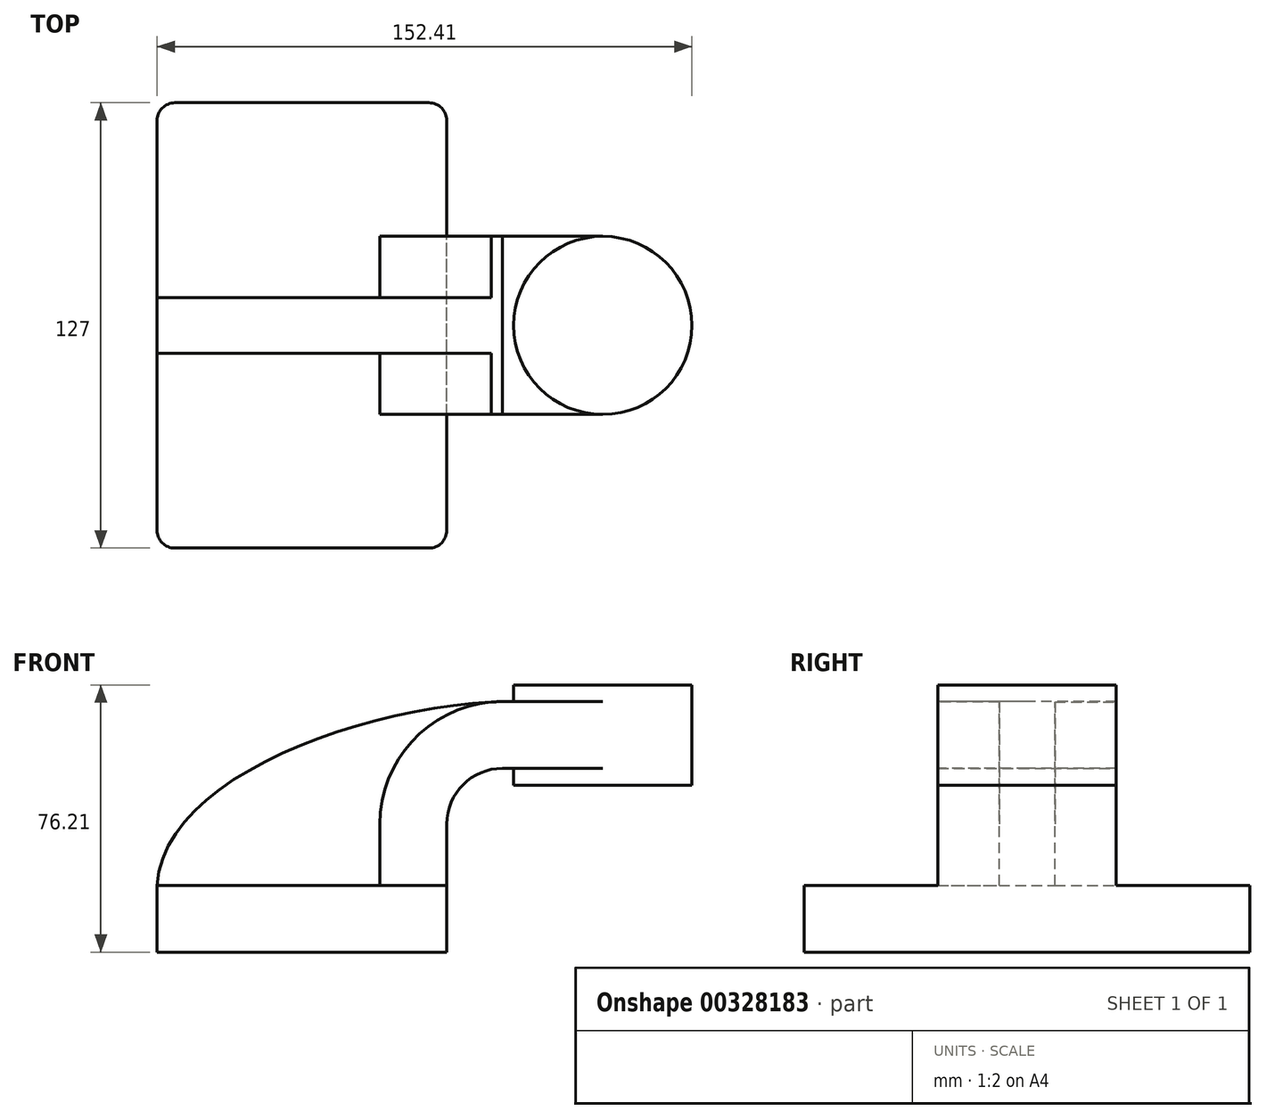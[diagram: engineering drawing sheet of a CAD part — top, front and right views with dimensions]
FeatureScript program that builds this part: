
annotation { "Feature Type Name" : "Feature", "Feature Type Description" : "" }
export const myFeature = defineFeature(function(context is Context, id is Id, definition is map)
    precondition{}
    {
        {
            var Q0;
            Q0=qCreatedBy(makeId("Front.planeOp"),FACE);
            var sketch = newSketch(context, id + "F0", { "sketchPlane" : qUnion([Q0])});
            skLineSegment(sketch, "E0.rect.bottom", {"start": v(-41.28, 9.52) * mm, "end": v(41.28, 9.52) * mm});
            skLineSegment(sketch, "E0.rect.top", {"start": v(-41.28, -9.52) * mm, "end": v(41.28, -9.52) * mm});
            skLineSegment(sketch, "E0.rect.left", {"start": v(-41.28, 9.52) * mm, "end": v(-41.28, -9.52) * mm});
            skLineSegment(sketch, "E0.rect.right", {"start": v(41.28, 9.52) * mm, "end": v(41.28, -9.52) * mm});
            skPoint(sketch, "E0.rect.middle", {"position": v(0, 0) * mm});
            skLineSegment(sketch, "E1", {"start": v(41.28, 9.52) * mm, "end": v(41.28, 27) * mm});
            skArc(sketch, "E2", {"start": v(41.28, 27) * mm, "mid": v(45.92, 38.23) * mm, "end": v(57.15, 42.88) * mm});
            skLineSegment(sketch, "E3", {"start": v(57.15, 42.88) * mm, "end": v(85.72, 42.88) * mm});
            skLineSegment(sketch, "E4.rect.bottom", {"start": v(60.32, 38.1) * mm, "end": v(111.12, 38.1) * mm});
            skLineSegment(sketch, "E4.rect.top", {"start": v(60.32, 66.68) * mm, "end": v(111.12, 66.68) * mm});
            skLineSegment(sketch, "E4.rect.left", {"start": v(60.32, 38.1) * mm, "end": v(60.32, 66.68) * mm});
            skLineSegment(sketch, "E4.rect.right", {"start": v(111.13, 38.1) * mm, "end": v(111.12, 66.68) * mm});
            skPoint(sketch, "E4.rect.middle", {"position": v(85.72, 52.39) * mm});
            skLineSegment(sketch, "E5.0", {"start": v(57.15, 61.93) * mm, "end": v(85.72, 61.93) * mm});
            skArc(sketch, "E5.1", {"start": v(22.23, 27) * mm, "mid": v(32.45, 51.7) * mm, "end": v(57.15, 61.93) * mm});
            skLineSegment(sketch, "E5.2", {"start": v(22.23, 9.52) * mm, "end": v(22.23, 27) * mm});
            skLineSegment(sketch, "E6", {"start": v(85.72, 38.1) * mm, "end": v(85.72, 66.68) * mm});
            skFitSpline(sketch, "E7", {"points": [v(-41.28, 9.53) * mm, v(57.15, 61.93) * mm], "startDerivative": vector(5.2, 92.34) * mm, "endDerivative": vector(120.92, 4.22) * mm});
            skSolve(sketch);
        }
        {
            var Q0;
            Q0=makeQuery(id+"F0.imprint","IMPRINT",FACE,{"disambiguationData":[TD([[makeQuery(id+"F0.imprint","IMPRINT",EDGE,{"derivedFrom":sQuery(id+"F0.wireOp",EDGE,"E0.rect.top")}),1.0]])]});
            extrude(context, id + "F1", {"entities" : qUnion([Q0]), "endBound" : BoundingType.SYMMETRIC, "depth" : 127 * mm});
        }
        {
            var Q0;
            {var subQ9=sQuery(id+"F0.wireOp",EDGE,"E1");Q0=makeQuery(id+"F0.imprint","IMPRINT",FACE,{"disambiguationData":[TD([[makeQuery(id+"F0.imprint","IMPRINT",EDGE,{"derivedFrom":subQ9}),1.0]])]});}
            var Q1;
            {var subQ0=sQuery(id+"F0.wireOp",EDGE,"E6");var subQ1=sQuery(id+"F0.wireOp",EDGE,"E3");var subQ2=makeQuery(id+"F0.imprint","INTERSECT",VERTEX,{"derivedFrom":[subQ1,subQ0]});Q1=makeQuery(id+"F0.imprint","IMPRINT",FACE,{"disambiguationData":[TD([[makeQuery(id+"F0.imprint","IMPRINT",EDGE,{"disambiguationData":[TD([[subQ2,1.0]])],"derivedFrom":subQ1}),1.0]])]});}
            extrude(context, id + "F2", {"entities" : qUnion([Q0, Q1]), "operationType" : NewBodyOperationType.ADD, "endBound" : BoundingType.SYMMETRIC, "depth" : 50.8 * mm});
        }
        {
            var Q0;
            {var subQ3=sQuery(id+"F0.wireOp",EDGE,"E5.2");Q0=makeQuery(id+"F0.imprint","IMPRINT",FACE,{"disambiguationData":[TD([[makeQuery(id+"F0.imprint","IMPRINT",EDGE,{"derivedFrom":subQ3}),1.0]])]});}
            extrude(context, id + "F3", {"entities" : qUnion([Q0]), "operationType" : NewBodyOperationType.ADD, "endBound" : BoundingType.SYMMETRIC, "depth" : 15.88 * mm});
        }
        {
            var Q0;
            {var subQ5=sQuery(id+"F0.wireOp",EDGE,"E4.rect.right");Q0=makeQuery(id+"F0.imprint","IMPRINT",FACE,{"disambiguationData":[TD([[makeQuery(id+"F0.imprint","IMPRINT",EDGE,{"derivedFrom":subQ5}),1.0]])]});}
            var Q1;
            Q1=sQuery(id+"F0.wireOp",EDGE,"E6");
            revolve(context, id + "F4", {"operationType" : NewBodyOperationType.ADD, "entities" : qUnion([Q0]), "axis" : qUnion([Q1]), "revolveType" : RevolveType.FULL});
        }
        {
            var Q0;
            Q0=makeQuery(id+"F1.opExtrude","CAP_EDGE",EDGE,{"disambiguationData":[OSD([sQuery(id+"F0.wireOp",EDGE,"E0.rect.right")])],"isStart":false});
            var Q1;
            Q1=makeQuery(id+"F1.opExtrude","CAP_EDGE",EDGE,{"disambiguationData":[OSD([sQuery(id+"F0.wireOp",EDGE,"E0.rect.left")])],"isStart":false});
            var Q2;
            Q2=makeQuery(id+"F1.opExtrude","CAP_EDGE",EDGE,{"disambiguationData":[OSD([sQuery(id+"F0.wireOp",EDGE,"E0.rect.right")])],"isStart":true});
            var Q3;
            Q3=makeQuery(id+"F1.opExtrude","CAP_EDGE",EDGE,{"disambiguationData":[OSD([sQuery(id+"F0.wireOp",EDGE,"E0.rect.left")])],"isStart":true});
            fillet(context, id + "F5", {"entities" : qUnion([Q0, Q1, Q2, Q3]), "radius" : 5.08 * mm, "tangentPropagation" : true, "allowEdgeOverflow" : false});
        }
        {
            var Q0;
            Q0=makeQuery(id+"F4.opRevolve","SWEPT_FACE",FACE,{"disambiguationData":[OSD([sQuery(id+"F0.wireOp",EDGE,"E4.rect.top")])]});
            var sketch = newSketch(context, id + "F6", { "sketchPlane" : qUnion([Q0])});
            skCircle(sketch, "E8", {"center": v(85.72, 0) * mm, "radius": 9.69 * mm});
            skSolve(sketch);
        }
        {
            var Q0;
            Q0=sQuery(id+"F6.wireOp",EDGE,"E8");
            extrude(context, id + "F7", {"bodyType" : ToolBodyType.SURFACE, "surfaceEntities" : qUnion([Q0]), "depth" : 25.4 * mm, "offsetDistance" : 25.4 * mm});
        }
    });
